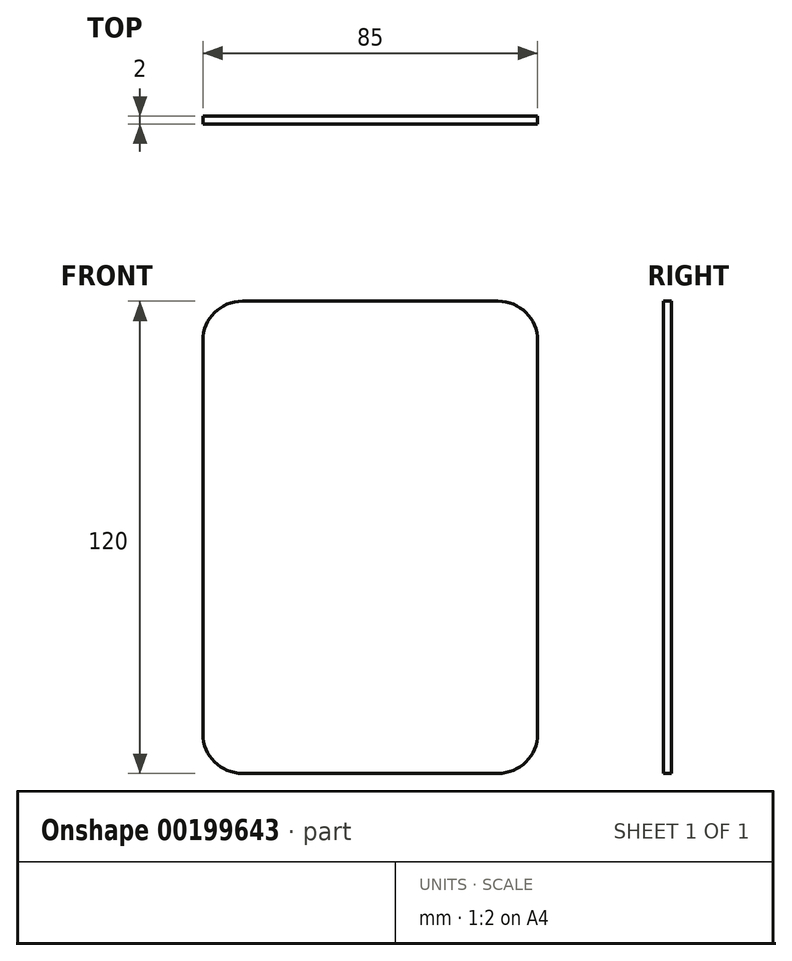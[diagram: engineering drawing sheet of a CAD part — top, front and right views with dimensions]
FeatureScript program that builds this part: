
annotation { "Feature Type Name" : "Feature", "Feature Type Description" : "" }
export const myFeature = defineFeature(function(context is Context, id is Id, definition is map)
    precondition{}
    {
        {
            var Q0;
            Q0=qCreatedBy(makeId("Front.planeOp"),FACE);
            var sketch = newSketch(context, id + "F0", { "sketchPlane" : qUnion([Q0])});
            skLineSegment(sketch, "E0.bottom", {"start": v(-32.5, 60) * mm, "end": v(32.5, 60) * mm});
            skLineSegment(sketch, "E0.top", {"start": v(-32.5, -60) * mm, "end": v(32.5, -60) * mm});
            skLineSegment(sketch, "E0.left", {"start": v(-42.5, 50) * mm, "end": v(-42.5, -50) * mm});
            skLineSegment(sketch, "E0.right", {"start": v(42.5, 50) * mm, "end": v(42.5, -50) * mm});
            skPoint(sketch, "E0.middle", {"position": v(0, 0) * mm});
            skArc(sketch, "E1.filletArc", {"start": v(-32.5, 60) * mm, "mid": v(-39.57, 57.07) * mm, "end": v(-42.5, 50) * mm});
            skArc(sketch, "E2.filletArc", {"start": v(42.5, 50) * mm, "mid": v(39.57, 57.07) * mm, "end": v(32.5, 60) * mm});
            skArc(sketch, "E3.filletArc", {"start": v(32.5, -60) * mm, "mid": v(39.57, -57.07) * mm, "end": v(42.5, -50) * mm});
            skArc(sketch, "E4.filletArc", {"start": v(-42.5, -50) * mm, "mid": v(-39.57, -57.07) * mm, "end": v(-32.5, -60) * mm});
            skSolve(sketch);
        }
        {
            var Q0;
            Q0 = qSketchRegion(id + "F0", true);
            extrude(context, id + "F1", {"entities" : qUnion([Q0]), "depth" : 2 * mm, "offsetDistance" : 25 * mm});
        }
    });
